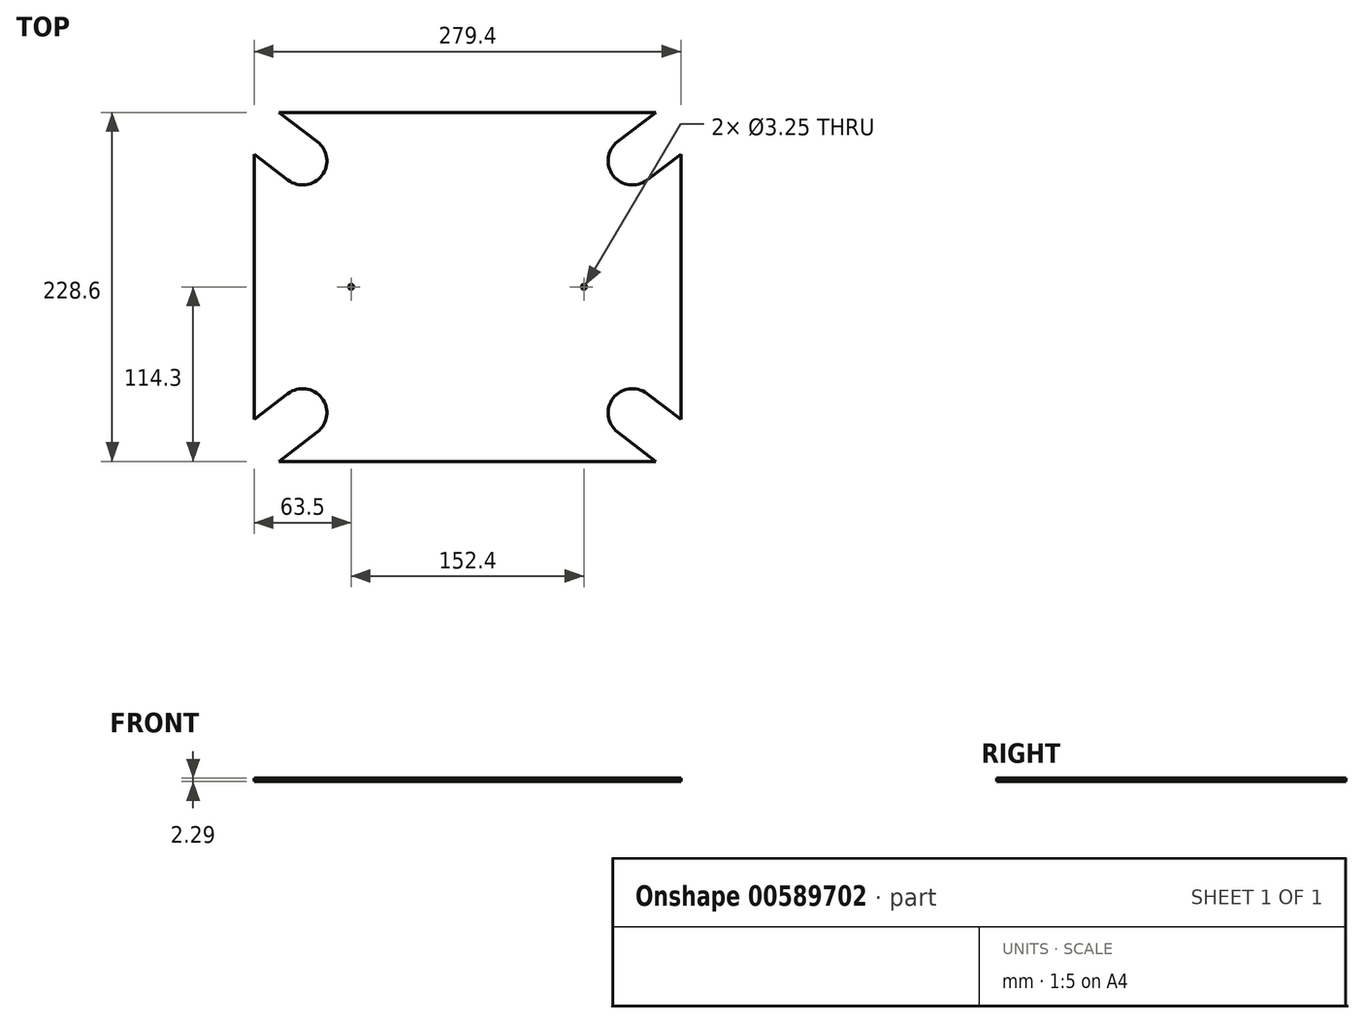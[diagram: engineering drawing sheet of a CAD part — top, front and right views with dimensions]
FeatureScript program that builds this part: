
annotation { "Feature Type Name" : "Feature", "Feature Type Description" : "" }
export const myFeature = defineFeature(function(context is Context, id is Id, definition is map)
    precondition{}
    {
        {
            var Q0;
            Q0=qCreatedBy(makeId("Top.planeOp"),FACE);
            var sketch = newSketch(context, id + "F0", { "sketchPlane" : qUnion([Q0])});
            skLineSegment(sketch, "E0.bottom", {"start": v(-139.7, 114.3) * mm, "end": v(139.7, 114.3) * mm});
            skLineSegment(sketch, "E0.top", {"start": v(-139.7, -114.3) * mm, "end": v(139.7, -114.3) * mm});
            skLineSegment(sketch, "E0.left", {"start": v(-139.7, 114.3) * mm, "end": v(-139.7, -114.3) * mm});
            skLineSegment(sketch, "E0.right", {"start": v(139.7, 114.3) * mm, "end": v(139.7, -114.3) * mm});
            skPoint(sketch, "E0.middle", {"position": v(0, 0) * mm});
            skSolve(sketch);
        }
        {
            var Q0;
            Q0 = qSketchRegion(id + "F0", true);
            extrude(context, id + "F1", {"entities" : qUnion([Q0]), "depth" : 2.3 * mm, "offsetDistance" : 25.4 * mm});
        }
        {
            var Q0;
            Q0=makeQuery(id+"F1.opExtrude","CAP_FACE",FACE,{"disambiguationData":[OSD([sQuery(id+"F0.wireOp",EDGE,"E0.bottom"),sQuery(id+"F0.wireOp",EDGE,"E0.top"),sQuery(id+"F0.wireOp",EDGE,"E0.left"),sQuery(id+"F0.wireOp",EDGE,"E0.right")])],"isStart":false});
            var sketch = newSketch(context, id + "F2", { "sketchPlane" : qUnion([Q0])});
            skLineSegment(sketch, "E1.bottom", {"start": v(-107.95, 82.55) * mm, "end": v(107.95, 82.55) * mm, "construction": true});
            skLineSegment(sketch, "E1.top", {"start": v(-107.95, -82.55) * mm, "end": v(107.95, -82.55) * mm, "construction": true});
            skLineSegment(sketch, "E1.left", {"start": v(-107.95, 82.55) * mm, "end": v(-107.95, -82.55) * mm, "construction": true});
            skLineSegment(sketch, "E1.right", {"start": v(107.95, 82.55) * mm, "end": v(107.95, -82.55) * mm, "construction": true});
            skPoint(sketch, "E1.middle", {"position": v(0, 0) * mm});
            skArc(sketch, "E2", {"start": v(-117.6, 69.94) * mm, "mid": v(-95.34, 72.9) * mm, "end": v(-98.3, 95.16) * mm});
            skArc(sketch, "E3", {"start": v(98.3, 95.16) * mm, "mid": v(95.34, 72.9) * mm, "end": v(117.6, 69.94) * mm});
            skArc(sketch, "E4", {"start": v(117.6, -69.94) * mm, "mid": v(95.34, -72.9) * mm, "end": v(98.3, -95.16) * mm});
            skArc(sketch, "E5", {"start": v(-98.3, -95.16) * mm, "mid": v(-95.34, -72.9) * mm, "end": v(-117.6, -69.94) * mm});
            skLineSegment(sketch, "E6", {"start": v(-107.95, 82.55) * mm, "end": v(107.95, -82.55) * mm, "construction": true});
            skLineSegment(sketch, "E7", {"start": v(107.95, 82.55) * mm, "end": v(-107.95, -82.55) * mm, "construction": true});
            skLineSegment(sketch, "E8.0", {"start": v(151.27, 135.66) * mm, "end": v(98.3, 95.16) * mm});
            skLineSegment(sketch, "E9.0", {"start": v(170.56, 110.44) * mm, "end": v(117.6, 69.94) * mm});
            skLineSegment(sketch, "E10.0", {"start": v(-170.56, 110.44) * mm, "end": v(-117.6, 69.94) * mm});
            skLineSegment(sketch, "E11.0", {"start": v(-151.27, 135.66) * mm, "end": v(-98.3, 95.16) * mm});
            skLineSegment(sketch, "E12.trimOffspring", {"start": v(0, 19.98) * mm, "end": v(-26.13, 0) * mm, "construction": true});
            skLineSegment(sketch, "E13.trimOffspring", {"start": v(0, 19.98) * mm, "end": v(26.13, 0) * mm, "construction": true});
            skLineSegment(sketch, "E14.trimOffspring", {"start": v(-26.13, 0) * mm, "end": v(0, -19.98) * mm, "construction": true});
            skLineSegment(sketch, "E15.trimOffspring", {"start": v(-117.6, -69.94) * mm, "end": v(-170.56, -110.44) * mm});
            skLineSegment(sketch, "E16.trimOffspring", {"start": v(-98.3, -95.16) * mm, "end": v(-151.27, -135.66) * mm});
            skLineSegment(sketch, "E17.trimOffspring", {"start": v(98.3, -95.16) * mm, "end": v(151.27, -135.66) * mm});
            skLineSegment(sketch, "E18.trimOffspring", {"start": v(117.6, -69.94) * mm, "end": v(170.56, -110.44) * mm});
            skLineSegment(sketch, "E19.trimOffspring", {"start": v(26.13, 0) * mm, "end": v(0, -19.98) * mm, "construction": true});
            skLineSegment(sketch, "E20", {"start": v(-151.27, -135.66) * mm, "end": v(-170.56, -110.44) * mm});
            skLineSegment(sketch, "E21", {"start": v(-151.27, 135.66) * mm, "end": v(-170.56, 110.44) * mm});
            skLineSegment(sketch, "E22", {"start": v(151.27, 135.66) * mm, "end": v(170.56, 110.44) * mm});
            skLineSegment(sketch, "E23", {"start": v(151.27, -135.66) * mm, "end": v(170.56, -110.44) * mm});
            skPoint(sketch, "E24.trimOffspring.end.orphan", {"position": v(170.56, 147.49) * mm});
            skPoint(sketch, "E25.right.start.orphan", {"position": v(170.56, -147.49) * mm});
            skPoint(sketch, "E25.left.start.orphan", {"position": v(-170.56, -147.49) * mm});
            skPoint(sketch, "E26.trimOffspring.end.orphan", {"position": v(-170.56, 147.49) * mm});
            skSolve(sketch);
        }
        {
            var Q0;
            Q0 = qSketchRegion(id + "F2", true);
            extrude(context, id + "F3", {"entities" : qUnion([Q0]), "operationType" : NewBodyOperationType.REMOVE, "endBound" : BoundingType.THROUGH_ALL, "oppositeDirection" : true, "depth" : 25.4 * mm, "offsetDistance" : 25.4 * mm});
        }
        {
            var Q0;
            Q0=makeQuery(id+"F1.opExtrude","CAP_FACE",FACE,{"disambiguationData":[OSD([sQuery(id+"F0.wireOp",EDGE,"E0.bottom"),sQuery(id+"F0.wireOp",EDGE,"E0.top"),sQuery(id+"F0.wireOp",EDGE,"E0.left"),sQuery(id+"F0.wireOp",EDGE,"E0.right")])],"isStart":false});
            var sketch = newSketch(context, id + "F4", { "sketchPlane" : qUnion([Q0])});
            skLineSegment(sketch, "E27", {"start": v(0, 0) * mm, "end": v(-139.7, 0) * mm, "construction": true});
            skLineSegment(sketch, "E28", {"start": v(0, 0) * mm, "end": v(139.7, 0) * mm, "construction": true});
            skPoint(sketch, "E29.center.orphan", {"position": v(-69.85, 0) * mm});
            skPoint(sketch, "E30.center.orphan", {"position": v(69.85, 0) * mm});
            skCircle(sketch, "E31", {"center": v(76.2, 0) * mm, "radius": 1.63 * mm});
            skLineSegment(sketch, "E32", {"start": v(0, 114.3) * mm, "end": v(0, -114.3) * mm, "construction": true});
            skCircle(sketch, "E33.MirrorC", {"center": v(-76.2, 0) * mm, "radius": 1.63 * mm});
            skSolve(sketch);
        }
        {
            var Q0;
            Q0 = qSketchRegion(id + "F4", true);
            extrude(context, id + "F5", {"entities" : qUnion([Q0]), "operationType" : NewBodyOperationType.REMOVE, "endBound" : BoundingType.THROUGH_ALL, "oppositeDirection" : true, "depth" : 25.4 * mm, "offsetDistance" : 25.4 * mm});
        }
    });
